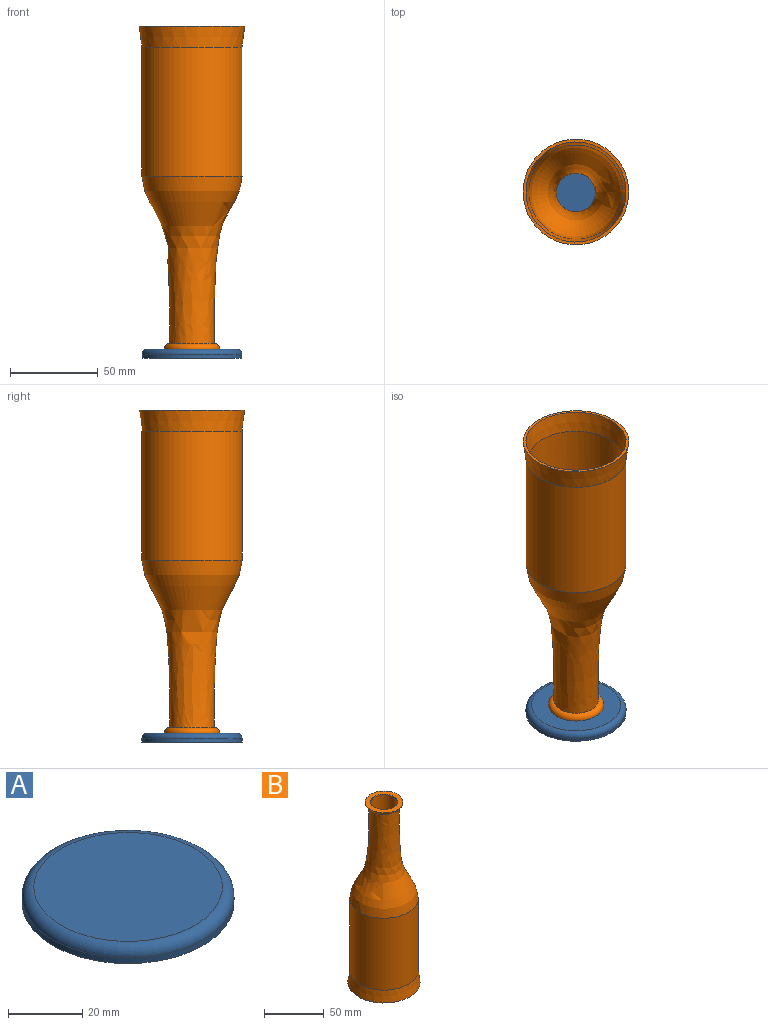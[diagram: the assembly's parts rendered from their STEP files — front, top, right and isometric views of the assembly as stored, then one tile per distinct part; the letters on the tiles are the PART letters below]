
ASSEMBLY  parts=2 mates=1
PART A: 6 faces, bbox 61.9x61.9x15.8 mm
  f0: cylinder r=28.57mm len=57.15mm, axis (0,0,1), area 342mm2, adj f1,f5
  f1: plane 57.21x57.21mm, normal (0,0,-1), area 687.6mm2, adj f0,f4
  f2: plane 50.8x50.8mm, normal (0,0,1), area 2026.8mm2, adj f5
  f3: plane 3.18x3.18mm, normal (0,0,-1), area 7.9mm2, adj f4
  f4: bspline ~55.38x55.38mm, area 1942.6mm2, adj f1,f3
  f5: torus R=25.4mm, axis (0,0,1), area 859.3mm2, adj f0,f2
PART B: 11 faces, bbox 60.3x60.3x187.5 mm
  f0: cylinder r=28.57mm len=73.63mm, axis (0,0,1), area 13220.1mm2, adj f5,f9
  f1: cylinder r=26.99mm len=73.63mm, axis (0,0,-1), area 12484.5mm2, adj f4,f10
  f2: revolved ~95.65x57.17mm, area 10373.4mm2, adj f3,f5
  f3: torus R=12.62mm, axis (0,0,-1), area 460mm2, adj f2,f8
  f4: revolved ~98.31x53.98mm, area 9546.9mm2, adj f1,f6
  f5: plane 57.17x57.17mm, normal (0,0,-1), area 1.9mm2, adj f0,f2
  f6: torus R=16.13mm, axis (0,0,-1), area 35.8mm2, adj f4,f8
  f7: plane 60.33x60.33mm, normal (0,0,-1), area 292.8mm2, adj f9,f10
  f8: plane 31.6x31.6mm, normal (0,0,1), area 398.5mm2, adj f3,f6
  f9: cone r=30.16mm half-angle=7.5deg, axis (0,0,-1), area 2244.3mm2, adj f0,f7
  f10: cone r=26.99mm half-angle=7.5deg, axis (0,0,-1), area 2124.2mm2, adj f1,f7
PLACE A t=(-0.03,-0.1,3.65)mm fixed
PLACE B rot(axis=(0,1,0),180deg) t=(-0.03,-0.1,204.07)mm
MATE planar B.f3 <-> A.f0  axis (0,0,-1) through (-0.03,-0.1,3.65)mm
